# Revit family: Toilet-Floor_Mount-Sloan-WETS-8029_Series
name_source: partatom
category: Plumbing Fixtures
revit_build: Autodesk Revit 2014 (Build: 20130308_1515(x64)
units: mm (PartAtom-declared; Revit-internal decimal feet)

## types (12) — shared parameters
ADA Compliant = Yes
Assembly Code = D2010110
CW Connection = Yes
CWFU = 10
Cold Water Connection Diameter = 1/2"
Cold Water Connection Radius = 1/4"
Default Elevation = 0"
Description = ADA floor mounted elongated pressure assist toilet
Fixture Color = White
HW Connection = No
Height = 29 5/8"
Length = 30 3/8"
Manufacturer = Sloan
Material = Vitreous China-Sloan-White
Mounting = Floor Mount
Price = Prices may vary. Please consult Manufacturer Representative for most up-to-date price list.
Spud Location = Top Spud
URL = https://www.sloan.com
Vent Connection = No
WFU = 10
Waste Connection = Yes
Waste Connection Diameter = 2 1/8"
Waste Connection Radius = 1 1/16"
Width = 18 1/8"
zero-valued in all types: HWFU

## per-type parameters (varying)
| type | Flush Volume(s)/Flow Rate(s) | Glaze | Left Handle | Model | Right Handle |
| WETS-8029.8016 | 1.0 gpf/3.8 Lpf | Conventional | Yes | WETS-8029.8016 | No |
| WETS-8029.8010 | 1.28 gpf/4.8 Lpf | Conventional | Yes | WETS-8029.8010 | No |
| WETS-8029.8013 | 1.6 gpf/6.0 Lpf | Conventional | Yes | WETS-8029.8013 | No |
| WETS-8029.8116 | 1.0 gpf/3.8 Lpf | Conventional | No | WETS-8029.8116 | Yes |
| WETS-8029.8110 | 1.28 gpf/4.8 Lpf | Conventional | No | WETS-8029.8110 | Yes |
| WETS-8029.8113 | 1.6 gpf/6.0 Lpf | Conventional | No | WETS-8029.8113 | Yes |
| WETS-8029.8010-STG | 1.28 gpf/4.8 Lpf | SloanTec | Yes | WETS-8029.8010-STG | No |
| WETS-8029.8013-STG | 1.6 gpf/6.0 Lpf | SloanTec | Yes | WETS-8029.8013 | No |
| WETS-8029.8016-STG | 1.0 gpf/3.8 Lpf | SloanTec | Yes | WETS-8029.8016-STG | No |
| WETS-8029.8113-STG | 1.6 gpf/6.0 Lpf | SloanTec | No | WETS-8029.8113-STG | Yes |
| WETS-8029.8116-STG | 1.0 gpf/3.8 Lpf | SloanTec | No | WETS-8029.8116-STG | Yes |
| WETS-8029.8110-STG | 1.28 gpf/4.8 Lpf | SloanTec | No | WETS-8029.8110-STG | Yes |

## geometry (parser evidence)
native form markers: Sweep x1
no freeform markers — native parametric forms only
